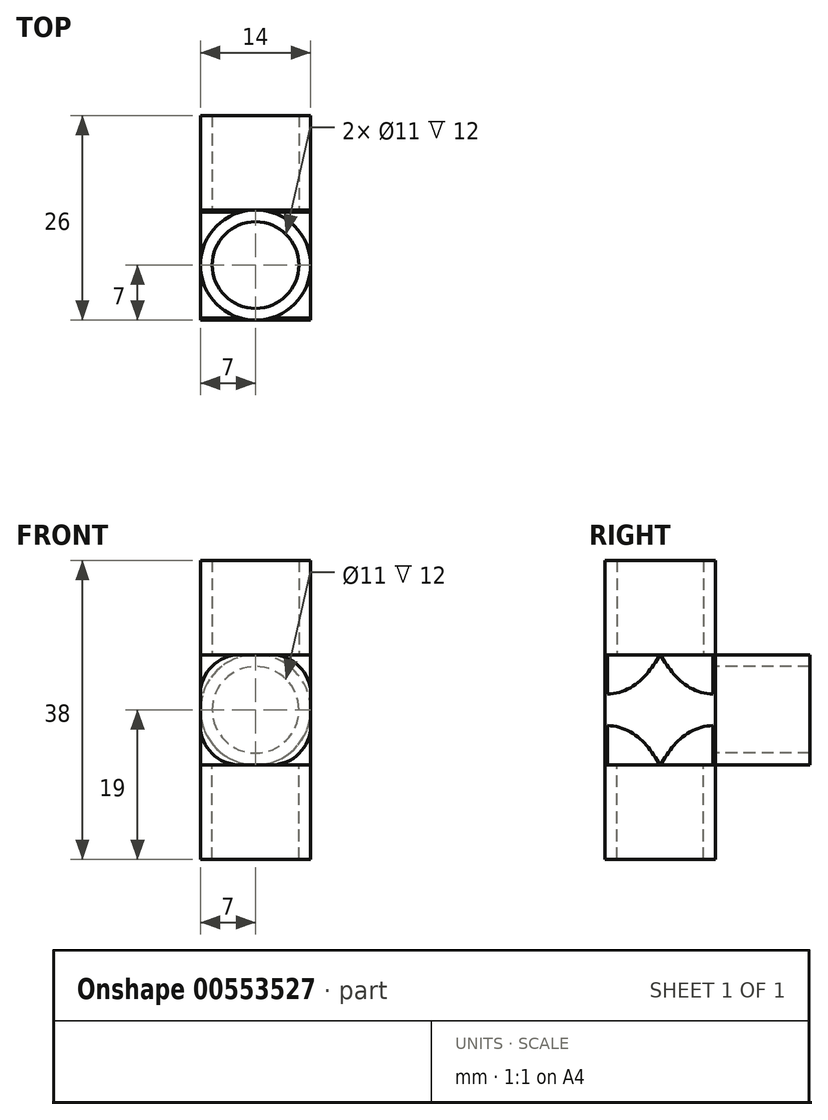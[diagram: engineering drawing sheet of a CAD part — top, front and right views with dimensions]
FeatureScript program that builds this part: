
annotation { "Feature Type Name" : "Feature", "Feature Type Description" : "" }
export const myFeature = defineFeature(function(context is Context, id is Id, definition is map)
    precondition{}
    {
        {
            var Q0;
            Q0=qCreatedBy(makeId("Top.planeOp"),FACE);
            var sketch = newSketch(context, id + "F0", { "sketchPlane" : qUnion([Q0])});
            skLineSegment(sketch, "E0.bottom", {"start": v(7, -7) * mm, "end": v(-7, -7) * mm});
            skLineSegment(sketch, "E0.top", {"start": v(7, 7) * mm, "end": v(-7, 7) * mm});
            skLineSegment(sketch, "E0.left", {"start": v(7, -7) * mm, "end": v(7, 7) * mm});
            skLineSegment(sketch, "E0.right", {"start": v(-7, -7) * mm, "end": v(-7, 7) * mm});
            skPoint(sketch, "E0.middle", {"position": v(0, 0) * mm});
            skSolve(sketch);
        }
        {
            var Q0;
            Q0=makeQuery(id+"F0.imprint","IMPRINT",FACE,{"disambiguationData":[TD([[makeQuery(id+"F0.imprint","IMPRINT",EDGE,{"derivedFrom":sQuery(id+"F0.wireOp",EDGE,"E0.bottom")}),-1.0]])]});
            extrude(context, id + "F1", {"entities" : qUnion([Q0]), "depth" : 14 * mm, "offsetDistance" : 25 * mm});
        }
        {
            var Q0;
            Q0=makeQuery(id+"F1.opExtrude","CAP_FACE",FACE,{"disambiguationData":[OSD([sQuery(id+"F0.wireOp",EDGE,"E0.bottom"),sQuery(id+"F0.wireOp",EDGE,"E0.top"),sQuery(id+"F0.wireOp",EDGE,"E0.left"),sQuery(id+"F0.wireOp",EDGE,"E0.right")])],"isStart":false});
            var sketch = newSketch(context, id + "F2", { "sketchPlane" : qUnion([Q0])});
            skCircle(sketch, "E1", {"center": v(0, 0) * mm, "radius": 7 * mm});
            skCircle(sketch, "E2", {"center": v(0, 0) * mm, "radius": 5.5 * mm});
            skSolve(sketch);
        }
        {
            var Q0;
            Q0=makeQuery(id+"F1.opExtrude","CAP_FACE",FACE,{"disambiguationData":[OSD([sQuery(id+"F0.wireOp",EDGE,"E0.bottom"),sQuery(id+"F0.wireOp",EDGE,"E0.top"),sQuery(id+"F0.wireOp",EDGE,"E0.left"),sQuery(id+"F0.wireOp",EDGE,"E0.right")])],"isStart":true});
            var sketch = newSketch(context, id + "F3", { "sketchPlane" : qUnion([Q0])});
            skCircle(sketch, "E3", {"center": v(0, 0) * mm, "radius": 7 * mm});
            skCircle(sketch, "E4", {"center": v(0, 0) * mm, "radius": 5.5 * mm});
            skSolve(sketch);
        }
        {
            var Q0;
            Q0=makeQuery(id+"F2.imprint","IMPRINT",FACE,{"disambiguationData":[TD([[makeQuery(id+"F2.imprint","IMPRINT",EDGE,{"derivedFrom":sQuery(id+"F2.wireOp",EDGE,"E2")}),-1.0]])]});
            extrude(context, id + "F4", {"entities" : qUnion([Q0]), "operationType" : NewBodyOperationType.ADD, "depth" : 12 * mm, "offsetDistance" : 25 * mm});
        }
        {
            var Q0;
            Q0=makeQuery(id+"F3.imprint","IMPRINT",FACE,{"disambiguationData":[TD([[makeQuery(id+"F3.imprint","IMPRINT",EDGE,{"derivedFrom":sQuery(id+"F3.wireOp",EDGE,"E4")}),-1.0]])]});
            extrude(context, id + "F5", {"entities" : qUnion([Q0]), "operationType" : NewBodyOperationType.ADD, "depth" : 12 * mm, "offsetDistance" : 25 * mm});
        }
        {
            var Q0;
            Q0=makeQuery(id+"F1.opExtrude","SWEPT_FACE",FACE,{"disambiguationData":[OSD([sQuery(id+"F0.wireOp",EDGE,"E0.top")])]});
            var sketch = newSketch(context, id + "F6", { "sketchPlane" : qUnion([Q0])});
            skLineSegment(sketch, "E5", {"start": v(7, 0) * mm, "end": v(7, 14) * mm});
            skCircle(sketch, "E6", {"center": v(0, 7) * mm, "radius": 7 * mm});
            skCircle(sketch, "E7", {"center": v(0, 7) * mm, "radius": 5.5 * mm});
            skSolve(sketch);
        }
        {
            var Q0;
            Q0=makeQuery(id+"F6.imprint","IMPRINT",FACE,{"disambiguationData":[TD([[makeQuery(id+"F6.imprint","IMPRINT",EDGE,{"derivedFrom":sQuery(id+"F6.wireOp",EDGE,"E7")}),-1.0]])]});
            extrude(context, id + "F7", {"entities" : qUnion([Q0]), "operationType" : NewBodyOperationType.ADD, "depth" : 12 * mm, "offsetDistance" : 25 * mm});
        }
        {
            var Q0;
            {var subQ0=sQuery(id+"F0.wireOp",EDGE,"E0.right");var subQ1=sQuery(id+"F0.wireOp",EDGE,"E0.top");Q0=makeQuery(id+"F4.boolean.opBoolean","SPLIT",EDGE,{"disambiguationData":[TD([makeQuery(id+"F1.opExtrude","SWEPT_FACE",FACE,{"disambiguationData":[OSD([subQ1])]})])],"derivedFrom":makeQuery(id+"F1.opExtrude","CAP_EDGE",EDGE,{"disambiguationData":[OSD([subQ0])],"isStart":false})});}
            fillet(context, id + "F8", {"entities" : qUnion([Q0]), "radius" : 5 * mm, "tangentPropagation" : true, "allowEdgeOverflow" : false});
        }
        {
            var Q0;
            {var subQ0=sQuery(id+"F0.wireOp",EDGE,"E0.right");var subQ1=sQuery(id+"F0.wireOp",EDGE,"E0.top");Q0=makeQuery(id+"F5.boolean.opBoolean","SPLIT",EDGE,{"disambiguationData":[TD([makeQuery(id+"F1.opExtrude","SWEPT_FACE",FACE,{"disambiguationData":[OSD([subQ1])]})])],"derivedFrom":makeQuery(id+"F1.opExtrude","CAP_EDGE",EDGE,{"disambiguationData":[OSD([subQ0])],"isStart":true})});}
            fillet(context, id + "F9", {"entities" : qUnion([Q0]), "radius" : 5 * mm, "tangentPropagation" : true, "allowEdgeOverflow" : false});
        }
        {
            var Q0;
            {var subQ0=sQuery(id+"F0.wireOp",EDGE,"E0.bottom");var subQ1=sQuery(id+"F0.wireOp",EDGE,"E0.left");Q0=makeQuery(id+"F4.boolean.opBoolean","SPLIT",EDGE,{"disambiguationData":[TD([makeQuery(id+"F1.opExtrude","SWEPT_FACE",FACE,{"disambiguationData":[OSD([subQ0])]})])],"derivedFrom":makeQuery(id+"F1.opExtrude","CAP_EDGE",EDGE,{"disambiguationData":[OSD([subQ1])],"isStart":false})});}
            fillet(context, id + "F10", {"entities" : qUnion([Q0]), "radius" : 5 * mm, "tangentPropagation" : true, "allowEdgeOverflow" : false});
        }
        {
            var Q0;
            {var subQ0=sQuery(id+"F0.wireOp",EDGE,"E0.left");var subQ1=sQuery(id+"F0.wireOp",EDGE,"E0.top");Q0=makeQuery(id+"F5.boolean.opBoolean","SPLIT",EDGE,{"disambiguationData":[TD([makeQuery(id+"F1.opExtrude","SWEPT_FACE",FACE,{"disambiguationData":[OSD([subQ1])]})])],"derivedFrom":makeQuery(id+"F1.opExtrude","CAP_EDGE",EDGE,{"disambiguationData":[OSD([subQ0])],"isStart":true})});}
            fillet(context, id + "F11", {"entities" : qUnion([Q0]), "radius" : 5 * mm, "tangentPropagation" : true, "allowEdgeOverflow" : false});
        }
    });
